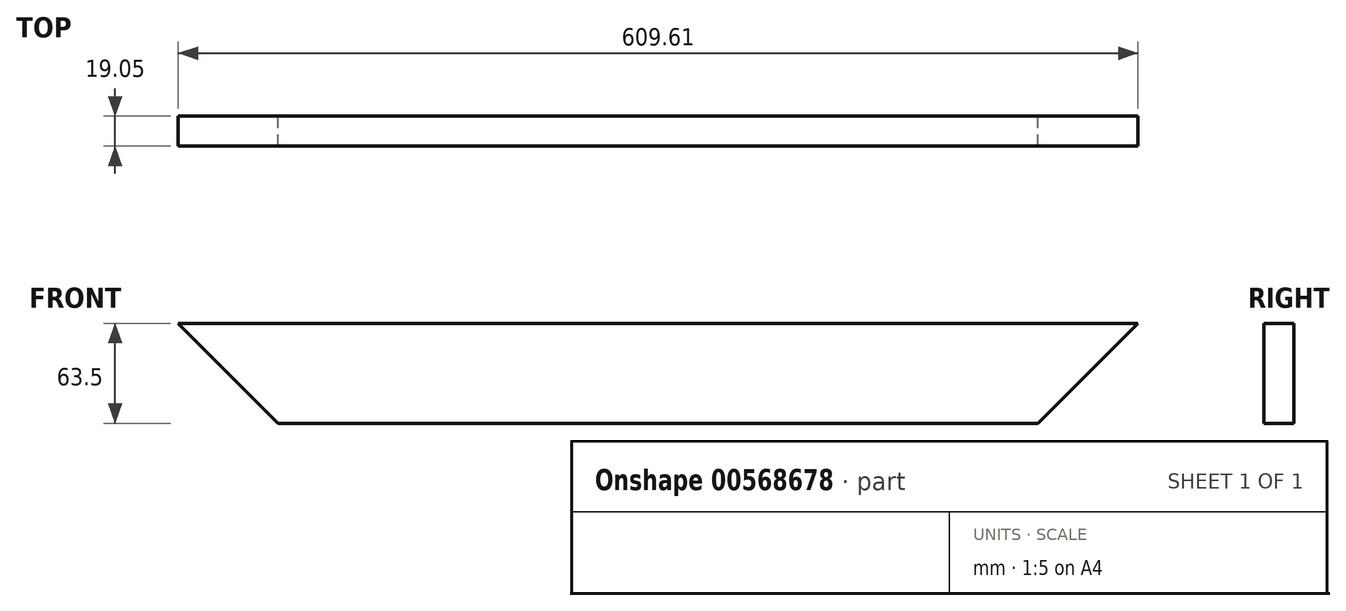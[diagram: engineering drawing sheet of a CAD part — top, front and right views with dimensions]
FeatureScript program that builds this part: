
annotation { "Feature Type Name" : "Feature", "Feature Type Description" : "" }
export const myFeature = defineFeature(function(context is Context, id is Id, definition is map)
    precondition{}
    {
        {
            var Q0;
            Q0=qCreatedBy(makeId("Front.planeOp"),FACE);
            var sketch = newSketch(context, id + "F0", { "sketchPlane" : qUnion([Q0])});
            skLineSegment(sketch, "E0.bottom", {"start": v(206.37, 31.75) * mm, "end": v(-403.23, 31.75) * mm});
            skLineSegment(sketch, "E0.top", {"start": v(142.87, -31.75) * mm, "end": v(-339.73, -31.75) * mm});
            skPoint(sketch, "E0.middle", {"position": v(0, 0) * mm});
            skLineSegment(sketch, "E1", {"start": v(-403.23, 31.75) * mm, "end": v(-339.73, -31.75) * mm});
            skLineSegment(sketch, "E2", {"start": v(206.38, 31.75) * mm, "end": v(142.87, -31.75) * mm});
            skSolve(sketch);
        }
        {
            var Q0;
            Q0=makeQuery(id+"F0.imprint","IMPRINT",FACE,{"disambiguationData":[TD([[makeQuery(id+"F0.imprint","IMPRINT",EDGE,{"derivedFrom":sQuery(id+"F0.wireOp",EDGE,"E0.bottom")}),1.0]])]});
            extrude(context, id + "F1", {"entities" : qUnion([Q0]), "depth" : 19.05 * mm, "offsetDistance" : 25.4 * mm});
        }
    });
